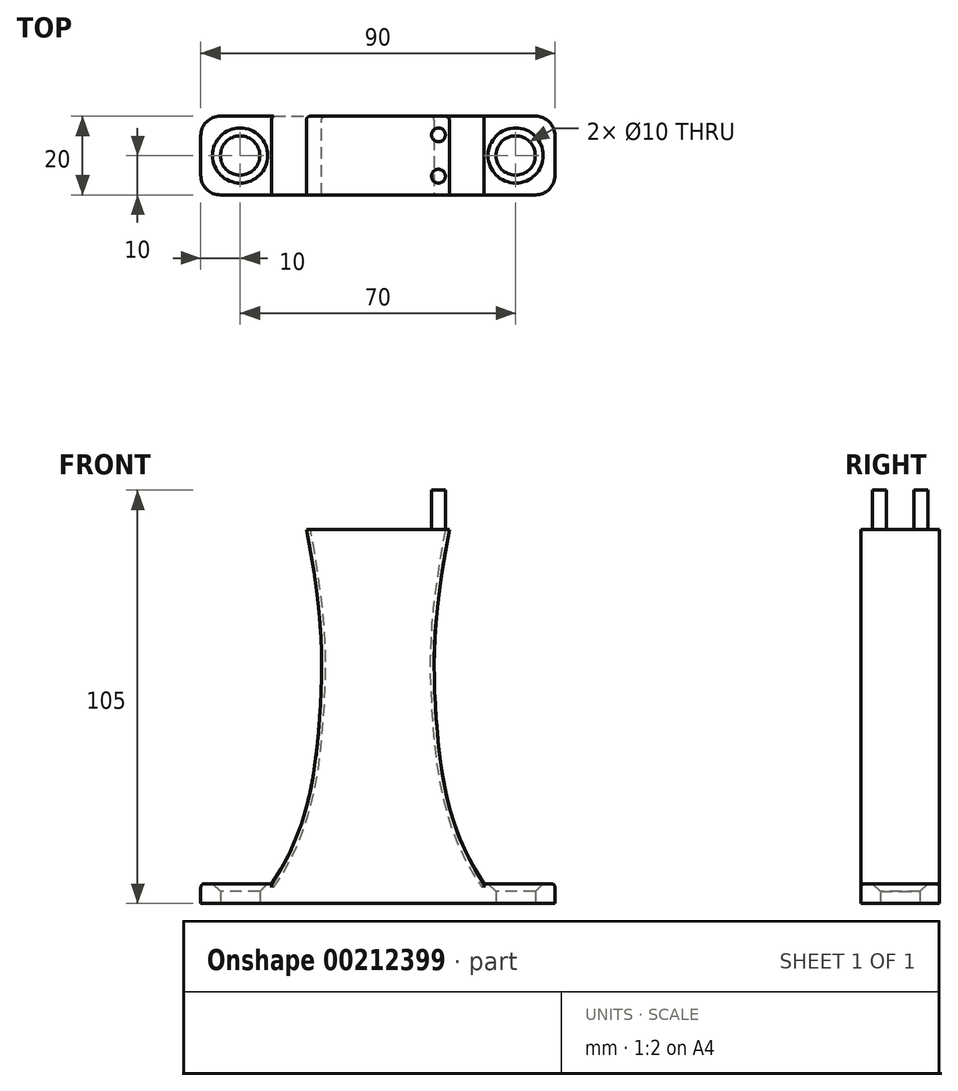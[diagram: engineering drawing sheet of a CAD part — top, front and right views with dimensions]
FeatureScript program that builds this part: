
annotation { "Feature Type Name" : "Feature", "Feature Type Description" : "" }
export const myFeature = defineFeature(function(context is Context, id is Id, definition is map)
    precondition{}
    {
        {
            var Q0;
            Q0=qCreatedBy(makeId("Top.planeOp"),FACE);
            var sketch = newSketch(context, id + "F0", { "sketchPlane" : qUnion([Q0])});
            skLineSegment(sketch, "E0.bottom", {"start": v(-40, 10) * mm, "end": v(40, 10) * mm});
            skLineSegment(sketch, "E0.top", {"start": v(-40, -10) * mm, "end": v(40, -10) * mm});
            skLineSegment(sketch, "E0.left", {"start": v(-45, 5) * mm, "end": v(-45, -5) * mm});
            skLineSegment(sketch, "E0.right", {"start": v(45, 5) * mm, "end": v(45, -5) * mm});
            skPoint(sketch, "E0.middle", {"position": v(0, 0) * mm});
            skCircle(sketch, "E1", {"center": v(-35, 0) * mm, "radius": 5 * mm});
            skCircle(sketch, "E2", {"center": v(35, 0) * mm, "radius": 5 * mm});
            skPoint(sketch, "E3.visualSharp", {"position": v(-45, 10) * mm});
            skArc(sketch, "E3.filletArc", {"start": v(-40, 10) * mm, "mid": v(-43.54, 8.54) * mm, "end": v(-45, 5) * mm});
            skPoint(sketch, "E4.visualSharp", {"position": v(-45, -10) * mm});
            skArc(sketch, "E4.filletArc", {"start": v(-45, -5) * mm, "mid": v(-43.54, -8.54) * mm, "end": v(-40, -10) * mm});
            skPoint(sketch, "E5.visualSharp", {"position": v(45, -10) * mm});
            skArc(sketch, "E5.filletArc", {"start": v(40, -10) * mm, "mid": v(43.54, -8.54) * mm, "end": v(45, -5) * mm});
            skPoint(sketch, "E6.visualSharp", {"position": v(45, 10) * mm});
            skArc(sketch, "E6.filletArc", {"start": v(45, 5) * mm, "mid": v(43.54, 8.54) * mm, "end": v(40, 10) * mm});
            skSolve(sketch);
        }
        {
            var Q0;
            Q0=makeQuery(id+"F0.imprint","IMPRINT",FACE,{"disambiguationData":[TD([[makeQuery(id+"F0.imprint","IMPRINT",EDGE,{"derivedFrom":sQuery(id+"F0.wireOp",EDGE,"E0.left")}),1.0]])]});
            var Q1;
            {var subQ0=sQuery(id+"F0.wireOp",EDGE,"apP93GuD-basS-9NN3-Wu4T-gJhYNzETebaI");Q1=makeQuery(id+"F0.imprint","IMPRINT",FACE,{"disambiguationData":[TD([[makeQuery(id+"F0.imprint","IMPRINT",EDGE,{"derivedFrom":subQ0}),1.0]])]});}
            var Q2;
            Q2=makeQuery(id+"F0.imprint","IMPRINT",FACE,{"disambiguationData":[TD([[makeQuery(id+"F0.imprint","IMPRINT",EDGE,{"derivedFrom":sQuery(id+"F0.wireOp",EDGE,"E0.right")}),-1.0]])]});
            extrude(context, id + "F1", {"entities" : qUnion([Q0, Q1, Q2]), "depth" : 5 * mm});
        }
        {
            var Q0;
            Q0=makeQuery(id+"F1.opExtrude","CAP_FACE",FACE,{"disambiguationData":[OSD([sQuery(id+"F0.wireOp",EDGE,"E0.bottom"),sQuery(id+"F0.wireOp",EDGE,"E0.top"),sQuery(id+"F0.wireOp",EDGE,"E0.left"),sQuery(id+"F0.wireOp",EDGE,"E0.right"),sQuery(id+"F0.wireOp",EDGE,"E1"),sQuery(id+"F0.wireOp",EDGE,"E2"),sQuery(id+"F0.wireOp",EDGE,"E3.filletArc"),sQuery(id+"F0.wireOp",EDGE,"E4.filletArc"),sQuery(id+"F0.wireOp",EDGE,"E5.filletArc"),sQuery(id+"F0.wireOp",EDGE,"E6.filletArc")])],"isStart":false});
            var sketch = newSketch(context, id + "F2", { "sketchPlane" : qUnion([Q0])});
            skLineSegment(sketch, "E7.bottom", {"start": v(27, -10) * mm, "end": v(-27, -10) * mm});
            skLineSegment(sketch, "E7.top", {"start": v(27, 10) * mm, "end": v(-27, 10) * mm});
            skLineSegment(sketch, "E7.left", {"start": v(27, -10) * mm, "end": v(27, 10) * mm});
            skLineSegment(sketch, "E7.right", {"start": v(-27, -10) * mm, "end": v(-27, 10) * mm});
            skPoint(sketch, "E7.middle", {"position": v(0, 0) * mm});
            skSolve(sketch);
        }
        {
            var Q0;
            Q0=makeQuery(id+"F2.imprint","IMPRINT",FACE,{"disambiguationData":[TD([[makeQuery(id+"F2.imprint","IMPRINT",EDGE,{"derivedFrom":sQuery(id+"F2.wireOp",EDGE,"E7.bottom")}),1.0]])]});
            extrude(context, id + "F3", {"entities" : qUnion([Q0]), "operationType" : NewBodyOperationType.ADD, "depth" : 100 * mm});
        }
        {
            var Q0;
            Q0=makeQuery(id+"F3.boolean.opBoolean","MERGE",FACE,{"derivedFrom":[makeQuery(id+"F1.opExtrude","SWEPT_FACE",FACE,{"disambiguationData":[OSD([sQuery(id+"F0.wireOp",EDGE,"E0.top")])]}),makeQuery(id+"F3.opExtrude","SWEPT_FACE",FACE,{"disambiguationData":[OSD([sQuery(id+"F2.wireOp",EDGE,"E7.bottom")])]})]});
            var sketch = newSketch(context, id + "F4", { "sketchPlane" : qUnion([Q0])});
            skCircle(sketch, "E8", {"center": v(0, 105) * mm, "radius": 5 * mm});
            skFitSpline(sketch, "E9", {"points": [v(-27, 5) * mm, v(-14.67, 49.48) * mm, v(-20.14, 105) * mm], "startDerivative": vector(62.44, 89.46) * mm, "endDerivative": vector(-35.53, 170.38) * mm});
            skFitSpline(sketch, "E10.MirrorCS", {"points": [v(27, 5) * mm, v(14.67, 49.48) * mm, v(20.14, 105) * mm], "startDerivative": vector(-62.44, 89.46) * mm, "endDerivative": vector(35.53, 170.38) * mm});
            skSolve(sketch);
        }
        {
            var Q0;
            Q0=makeQuery(id+"FClc3PCctBsu9z6_1.boolean.opBoolean","COPY",EDGE,{"derivedFrom":makeQuery(id+"FClc3PCctBsu9z6_1.opExtrude","CAP_EDGE",EDGE,{"disambiguationData":[OSD([sQuery(id+"F4.wireOp",EDGE,"66c0a1e7-aa96-4d85-9e5c-27c3072577fe0.MirrorCS")])],"isStart":true})});
            var Q1;
            Q1=makeQuery(id+"FClc3PCctBsu9z6_1.boolean.opBoolean","INTERSECT",EDGE,{"derivedFrom":[makeQuery(id+"F3.boolean.opBoolean","MERGE",FACE,{"derivedFrom":[makeQuery(id+"F1.opExtrude","SWEPT_FACE",FACE,{"disambiguationData":[OSD([sQuery(id+"F0.wireOp",EDGE,"E0.bottom")])]}),makeQuery(id+"F3.opExtrude","SWEPT_FACE",FACE,{"disambiguationData":[OSD([sQuery(id+"F2.wireOp",EDGE,"E7.top")])]})]}),makeQuery(id+"FClc3PCctBsu9z6_1.opExtrude","SWEPT_FACE",FACE,{"disambiguationData":[OSD([sQuery(id+"F4.wireOp",EDGE,"66c0a1e7-aa96-4d85-9e5c-27c3072577fe0.MirrorCS")])]})]});
            var Q2;
            {var subQ0=sQuery(id+"F0.wireOp",EDGE,"E6.filletArc");var subQ1=sQuery(id+"F0.wireOp",EDGE,"E0.bottom");Q2=makeQuery(id+"F3.boolean.opBoolean","SPLIT",EDGE,{"disambiguationData":[TD([makeQuery(id+"F1.opExtrude","SWEPT_FACE",FACE,{"disambiguationData":[OSD([subQ0])]})])],"derivedFrom":makeQuery(id+"F1.opExtrude","CAP_EDGE",EDGE,{"disambiguationData":[OSD([subQ1])],"isStart":false})});}
            var Q3;
            {var subQ0=sQuery(id+"F0.wireOp",EDGE,"E4.filletArc");var subQ1=sQuery(id+"F0.wireOp",EDGE,"E0.top");Q3=makeQuery(id+"F3.boolean.opBoolean","SPLIT",EDGE,{"disambiguationData":[TD([makeQuery(id+"F1.opExtrude","SWEPT_FACE",FACE,{"disambiguationData":[OSD([subQ0])]})])],"derivedFrom":makeQuery(id+"F1.opExtrude","CAP_EDGE",EDGE,{"disambiguationData":[OSD([subQ1])],"isStart":false})});}
            var Q4;
            Q4=makeQuery(id+"FClc3PCctBsu9z6_1.boolean.opBoolean","COPY",EDGE,{"derivedFrom":makeQuery(id+"FClc3PCctBsu9z6_1.opExtrude","CAP_EDGE",EDGE,{"disambiguationData":[OSD([sQuery(id+"F4.wireOp",EDGE,"bc4d347b-1d29-43ac-a498-6006287adc93")])],"isStart":true})});
            var Q5;
            Q5=makeQuery(id+"FClc3PCctBsu9z6_1.boolean.opBoolean","INTERSECT",EDGE,{"derivedFrom":[makeQuery(id+"F3.boolean.opBoolean","MERGE",FACE,{"derivedFrom":[makeQuery(id+"F1.opExtrude","SWEPT_FACE",FACE,{"disambiguationData":[OSD([sQuery(id+"F0.wireOp",EDGE,"E0.bottom")])]}),makeQuery(id+"F3.opExtrude","SWEPT_FACE",FACE,{"disambiguationData":[OSD([sQuery(id+"F2.wireOp",EDGE,"E7.top")])]})]}),makeQuery(id+"FClc3PCctBsu9z6_1.opExtrude","SWEPT_FACE",FACE,{"disambiguationData":[OSD([sQuery(id+"F4.wireOp",EDGE,"bc4d347b-1d29-43ac-a498-6006287adc93")])]})]});
            fillet(context, id + "F5", {"entities" : qUnion([Q0, Q1, Q2, Q3, Q4, Q5]), "radius" : 1 * mm, "tangentPropagation" : true, "allowEdgeOverflow" : false});
        }
        {
            var Q0;
            {var subQ0=sQuery(id+"F2.wireOp",EDGE,"E7.top");var subQ1=sQuery(id+"F2.wireOp",EDGE,"E7.bottom");Q0=makeQuery(id+"FClc3PCctBsu9z6_1.boolean.opBoolean","SPLIT",FACE,{"disambiguationData":[TD([makeQuery(id+"FClc3PCctBsu9z6_1.opExtrude","SWEPT_FACE",FACE,{"disambiguationData":[OSD([sQuery(id+"F4.wireOp",EDGE,"bc4d347b-1d29-43ac-a498-6006287adc93")])]})])],"derivedFrom":makeQuery(id+"F3.opExtrude","CAP_FACE",FACE,{"disambiguationData":[OSD([subQ1,subQ0,sQuery(id+"F2.wireOp",EDGE,"E7.left"),sQuery(id+"F2.wireOp",EDGE,"E7.right")])],"isStart":false})});}
            var sketch = newSketch(context, id + "F6", { "sketchPlane" : qUnion([Q0])});
            skCircle(sketch, "E11", {"center": v(-15.4, 5.25) * mm, "radius": 1.75 * mm});
            skCircle(sketch, "E12", {"center": v(-15.4, -5.25) * mm, "radius": 1.75 * mm});
            skCircle(sketch, "E13.MirrorC", {"center": v(15.4, 5.25) * mm, "radius": 1.75 * mm});
            skCircle(sketch, "E14.MirrorC", {"center": v(15.4, -5.25) * mm, "radius": 1.75 * mm});
            skSolve(sketch);
        }
        {
            var Q0;
            Q0=makeQuery(id+"F6.imprint","IMPRINT",FACE,{"disambiguationData":[TD([[makeQuery(id+"F6.imprint","IMPRINT",EDGE,{"derivedFrom":sQuery(id+"F6.wireOp",EDGE,"E11")}),1.0]])]});
            var Q1;
            Q1=makeQuery(id+"F6.imprint","IMPRINT",FACE,{"disambiguationData":[TD([[makeQuery(id+"F6.imprint","IMPRINT",EDGE,{"derivedFrom":sQuery(id+"F6.wireOp",EDGE,"QkITlQbj-4w8x-jJN3-EXHF-ldyRhXvQetfI")}),1.0]])]});
            var Q2;
            Q2=makeQuery(id+"F6.imprint","IMPRINT",FACE,{"disambiguationData":[TD([[makeQuery(id+"F6.imprint","IMPRINT",EDGE,{"derivedFrom":sQuery(id+"F6.wireOp",EDGE,"E12")}),1.0]])]});
            var Q3;
            Q3=makeQuery(id+"F6.imprint","IMPRINT",FACE,{"disambiguationData":[TD([[makeQuery(id+"F6.imprint","IMPRINT",EDGE,{"derivedFrom":sQuery(id+"F6.wireOp",EDGE,"E13.MirrorC")}),-1.0]])]});
            var Q4;
            Q4=makeQuery(id+"F6.imprint","IMPRINT",FACE,{"disambiguationData":[TD([[makeQuery(id+"F6.imprint","IMPRINT",EDGE,{"derivedFrom":sQuery(id+"F6.wireOp",EDGE,"62c8c5fe-792d-47b8-89af-4f7ad2a674ef0.MirrorC")}),-1.0]])]});
            var Q5;
            Q5=makeQuery(id+"F6.imprint","IMPRINT",FACE,{"disambiguationData":[TD([[makeQuery(id+"F6.imprint","IMPRINT",EDGE,{"derivedFrom":sQuery(id+"F6.wireOp",EDGE,"E14.MirrorC")}),-1.0]])]});
            extrude(context, id + "F7", {"entities" : qUnion([Q0, Q1, Q2, Q3, Q4, Q5]), "operationType" : NewBodyOperationType.REMOVE, "oppositeDirection" : true, "depth" : 10 * mm});
        }
        {
            var Q0;
            Q0=makeQuery(id+"F1.opExtrude","CAP_EDGE",EDGE,{"disambiguationData":[OSD([sQuery(id+"F0.wireOp",EDGE,"E2")])],"isStart":false});
            var Q1;
            Q1=makeQuery(id+"F1.opExtrude","CAP_EDGE",EDGE,{"disambiguationData":[OSD([sQuery(id+"F0.wireOp",EDGE,"E1")])],"isStart":false});
            chamfer(context, id + "F8", {"entities" : qUnion([Q0, Q1]), "width" : 2 * mm, "tangentPropagation" : true});
        }
        {
            var Q0;
            {var subQ0=sQuery(id+"F4.wireOp",EDGE,"E9");Q0=makeQuery(id+"F4.imprint","IMPRINT",FACE,{"disambiguationData":[TD([[makeQuery(id+"F4.imprint","IMPRINT",EDGE,{"derivedFrom":subQ0}),1.0]])]});}
            var Q1;
            {var subQ0=sQuery(id+"F4.wireOp",EDGE,"E10.MirrorCS");Q1=makeQuery(id+"F4.imprint","IMPRINT",FACE,{"disambiguationData":[TD([[makeQuery(id+"F4.imprint","IMPRINT",EDGE,{"derivedFrom":subQ0}),-1.0]])]});}
            extrude(context, id + "F9", {"entities" : qUnion([Q0, Q1]), "operationType" : NewBodyOperationType.REMOVE, "oppositeDirection" : true, "depth" : 25 * mm});
        }
        {
            var Q0;
            {var subQ0=sQuery(id+"F4.wireOp",EDGE,"E8");var subQ1=makeQuery(id+"F3.opExtrude","CAP_EDGE",EDGE,{"disambiguationData":[OSD([sQuery(id+"F2.wireOp",EDGE,"E7.bottom")])],"isStart":false});var subQ2=makeQuery(id+"F4.imprint","INTERSECT",VERTEX,{"disambiguationData":[OD(0.0)],"derivedFrom":[subQ1,subQ0]});Q0=makeQuery(id+"F4.imprint","IMPRINT",FACE,{"disambiguationData":[TD([[makeQuery(id+"F4.imprint","IMPRINT",EDGE,{"disambiguationData":[TD([[subQ2,-1.0]])],"derivedFrom":subQ0}),1.0]])]});}
            extrude(context, id + "F10", {"entities" : qUnion([Q0]), "operationType" : NewBodyOperationType.REMOVE, "oppositeDirection" : true, "depth" : 25 * mm});
        }
        {
            var Q0;
            Q0=makeQuery(id+"F9.boolean.opBoolean","COPY",EDGE,{"derivedFrom":makeQuery(id+"F9.opExtrude","CAP_EDGE",EDGE,{"disambiguationData":[OSD([sQuery(id+"F4.wireOp",EDGE,"E9")])],"isStart":true})});
            var Q1;
            Q1=makeQuery(id+"F9.boolean.opBoolean","COPY",EDGE,{"derivedFrom":makeQuery(id+"F9.opExtrude","CAP_EDGE",EDGE,{"disambiguationData":[OSD([sQuery(id+"F4.wireOp",EDGE,"E10.MirrorCS")])],"isStart":true})});
            var Q2;
            Q2=makeQuery(id+"F9.boolean.opBoolean","INTERSECT",EDGE,{"derivedFrom":[makeQuery(id+"F3.boolean.opBoolean","MERGE",FACE,{"derivedFrom":[makeQuery(id+"F1.opExtrude","SWEPT_FACE",FACE,{"disambiguationData":[OSD([sQuery(id+"F0.wireOp",EDGE,"E0.bottom")])]}),makeQuery(id+"F3.opExtrude","SWEPT_FACE",FACE,{"disambiguationData":[OSD([sQuery(id+"F2.wireOp",EDGE,"E7.top")])]})]}),makeQuery(id+"F9.opExtrude","SWEPT_FACE",FACE,{"disambiguationData":[OSD([sQuery(id+"F4.wireOp",EDGE,"E10.MirrorCS")])]})]});
            var Q3;
            Q3=makeQuery(id+"F9.boolean.opBoolean","INTERSECT",EDGE,{"derivedFrom":[makeQuery(id+"F3.boolean.opBoolean","MERGE",FACE,{"derivedFrom":[makeQuery(id+"F1.opExtrude","SWEPT_FACE",FACE,{"disambiguationData":[OSD([sQuery(id+"F0.wireOp",EDGE,"E0.bottom")])]}),makeQuery(id+"F3.opExtrude","SWEPT_FACE",FACE,{"disambiguationData":[OSD([sQuery(id+"F2.wireOp",EDGE,"E7.top")])]})]}),makeQuery(id+"F9.opExtrude","SWEPT_FACE",FACE,{"disambiguationData":[OSD([sQuery(id+"F4.wireOp",EDGE,"E9")])]})]});
            fillet(context, id + "F11", {"entities" : qUnion([Q0, Q1, Q2, Q3]), "radius" : 1 * mm, "tangentPropagation" : true, "allowEdgeOverflow" : false});
        }
    });
